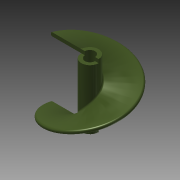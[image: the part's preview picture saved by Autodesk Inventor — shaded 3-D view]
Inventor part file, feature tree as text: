
AUTODESK INVENTOR PART (.ipt)
format: ipt  version: 2014 SP2 (Build 180246200, 246)  size: 262,656 bytes
history: native  units: mm
features: extrude x3, sketch x3, helix x1, fillet x1, projected_geometry x1
ambient origin geometry x8: Origin, YZ Plane, XZ Plane, XY Plane, X Axis, Y Axis, Z Axis, Center Point
bodies: Solid1 (feature_tree)
feature tree (9):
  extrude  "Extrusion1"  Depth=3.0mm
  helix  "Coil2"  [1 undecoded]
  extrude  "Extrusion5"  Depth=3.0mm
  fillet  "Fillet3"  [1 undecoded]
  extrude  "Extrusion6"  Depth=3.0mm
  sketch  "Sketch1"  dims[d0=8.5mm d1=3.0mm d2=53.0mm d3=0.0mm]
  projected_geometry  "Projected Loop1"
  sketch  "Sketch7"  dims[d17=25.5mm d18=3.0mm]
  sketch  "Sketch8"  dims[d19=50.0mm d20=10.0mm d21=10.0mm d22=0.0mm d23=90.0deg d24=90.0deg d25=0.0mm d26=0.0mm d29=0.0mm d39=1.3mm d40=3.0mm d41=0.0mm d42=3.0mm d43=0.0mm]
note: 2 required parameter values undecoded (feature->parameter linkage not recoverable at this tier; creation-order binding heuristic only, values carry confidence <= 0.55)
